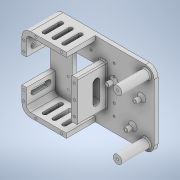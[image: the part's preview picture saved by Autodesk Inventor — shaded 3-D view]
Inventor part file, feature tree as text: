
AUTODESK INVENTOR PART (.ipt)
format: ipt  version: 2020 (Build 240168000, 168)  size: 406,016 bytes
history: native  units: mm
features: sketch x12, extrude x10, other x4, fillet x3, reference x2, hole x1, projected_geometry x1
ambient origin geometry x8: Origin, YZ Plane, XZ Plane, XY Plane, X Axis, Y Axis, Z Axis, Center Point
bodies: Solid1 (feature_tree)
feature tree (33):
  extrude  "Extrusion1"  Depth=130.0mm
  extrude  "Extrusion2"  Depth=15.0mm
  extrude  "Extrusion3"  Depth=15.0mm
  fillet  "Fillet1"  Radius=104.0mm
  extrude  "Extrusion4"  Depth=75.0mm
  extrude  "Extrusion5"  Depth=70.0mm
  sketch  "Sketch7"  dims[d17=7.5mm d18=35.0mm d19=50.0mm d20=0.0mm]
  extrude  "Extrusion6"  Depth=35.0mm
  fillet  "Fillet2"  Radius=50.0mm
  extrude  "Extrusion7"  Depth=40.0mm
  fillet  "Fillet3"  Radius=50.0mm
  hole  "Hole1"  [1 undecoded]
  extrude  "Extrusion8"  Depth=50.0mm TaperAngle=0.0deg
  extrude  "Extrusion9"  Depth=6.0mm
  extrude  "Extrusion10"  Depth=25.0mm
  sketch  "Sketch1"  dims[d0=180.0mm d1=130.0mm]
  sketch  "Sketch3"  dims[d2=7.0mm d3=0.0mm d9=15.0mm]
  sketch  "Sketch4"  dims[d10=15.0mm d11=15.0mm d12=104.0mm]
  sketch  "Sketch5"  dims[d13=52.0mm d14=75.0mm]
  projected_geometry  "Projected Loop1"
  sketch  "Sketch6"  dims[d15=12.0mm d16=70.0mm]
  sketch  "Sketch8"  dims[d21=46.0mm d22=40.0mm d23=50.0mm d24=0.0mm]
  reference  "Reference1"
  reference  "Reference2"
  sketch  "Sketch10"  dims[d25=28.0mm d26=2.0mm]
  sketch  "Sketch11"  dims[d27=8.0mm d28=50.0mm d29=0.0mm]
  sketch  "Sketch12"  dims[d30=4.0mm d31=6.0mm]
  sketch  "Sketch13"  dims[d32=25.0mm d33=25.0mm]
  sketch  "Sketch14"  dims[d34=45.0mm d35=3.5mm d36=8.0mm d37=3.5mm d38=17.0mm d39=6.0mm d40=6.0mm d41=3.5mm d42=17.0mm d43=3.5mm d44=10.0mm d45=0.0mm d46=10.0mm d47=0.0mm d48=2.0mm d49=7.0mm d50=12.0mm d51=0.0mm d52=4.0mm d53=4.0mm d54=6.0mm d55=6.3mm d56=2.0mm d57=90.0deg d58=5.0mm d59=20.594885mm d60=10.0mm d61=10.0mm d62=28.0mm d63=25.0mm d64=11.0mm d65=3.5mm d66=0.0mm d67=0.0mm d68=30.0mm d69=12.0mm d70=32.0mm d71=16.0mm d72=12.0mm d73=0.0mm d74=25.0mm d75=5.0mm d76=32.0mm d77=12.0mm d78=12.0mm d79=0.0mm]
  other  "<userpath>\Desktop\KangKangBalancing\KangKang.iam"
  other  "KangKang.iam"
  other  "Body-R:1"
  other  "bodyL:1"
note: 1 required parameter value undecoded (feature->parameter linkage not recoverable at this tier; creation-order binding heuristic only, values carry confidence <= 0.55)
